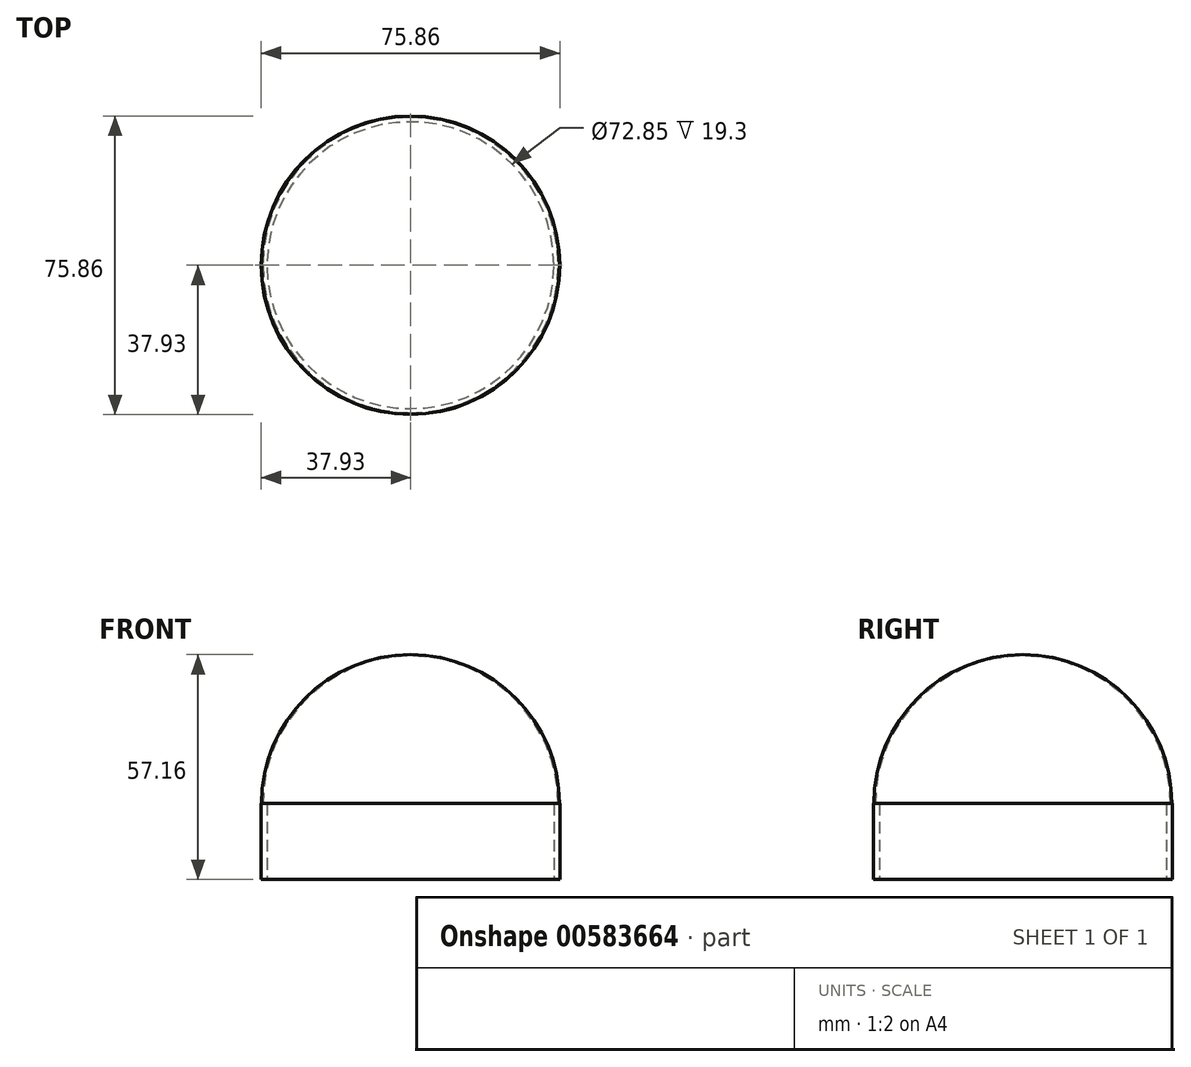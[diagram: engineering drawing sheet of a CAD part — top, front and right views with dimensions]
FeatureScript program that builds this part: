
annotation { "Feature Type Name" : "Feature", "Feature Type Description" : "" }
export const myFeature = defineFeature(function(context is Context, id is Id, definition is map)
    precondition{}
    {
        {
            var Q0;
            Q0=qCreatedBy(makeId("Top.planeOp"),FACE);
            var sketch = newSketch(context, id + "F0", { "sketchPlane" : qUnion([Q0])});
            skCircle(sketch, "E0", {"center": v(0, 0) * mm, "radius": 37.5 * mm});
            skSolve(sketch);
        }
        {
            var Q0;
            Q0=qCreatedBy(makeId("Top.planeOp"),FACE);
            var sketch = newSketch(context, id + "F1", { "sketchPlane" : qUnion([Q0])});
            skCircle(sketch, "E1", {"center": v(0, 0) * mm, "radius": 37.93 * mm});
            skSolve(sketch);
        }
        {
            var Q0;
            Q0 = qSketchRegion(id + "F1", true);
            var Q1;
            Q1=makeQuery(id+"F0.imprint","IMPRINT",FACE,{"disambiguationData":[TD([[makeQuery(id+"F0.imprint","IMPRINT",EDGE,{"derivedFrom":sQuery(id+"F0.wireOp",EDGE,"E0")}),1.0]])]});
            extrude(context, id + "F2", {"entities" : qUnion([Q0, Q1]), "depth" : 19.3 * mm, "offsetDistance" : 25 * mm});
        }
        {
            var Q0;
            Q0=makeQuery(id+"F2.opExtrude","CAP_FACE",FACE,{"disambiguationData":[OSD([sQuery(id+"F0.wireOp",EDGE,"E0")])],"isStart":false});
            var sketch = newSketch(context, id + "F3", { "sketchPlane" : qUnion([Q0])});
            skArc(sketch, "E2", {"start": v(0, -37.86) * mm, "mid": v(37.86, 0) * mm, "end": v(0, 37.86) * mm});
            skLineSegment(sketch, "E3", {"start": v(0, 46.44) * mm, "end": v(0, -50.35) * mm, "construction": true});
            skLineSegment(sketch, "E4", {"start": v(0, 37.86) * mm, "end": v(0, -37.86) * mm});
            skSolve(sketch);
        }
        {
            var Q0;
            {var subQ0=sQuery(id+"F3.wireOp",EDGE,"E2");Q0=makeQuery(id+"F3.imprint","IMPRINT",FACE,{"disambiguationData":[TD([[makeQuery(id+"F3.imprint","IMPRINT",EDGE,{"derivedFrom":subQ0}),1.0]])]});}
            var Q1;
            Q1=sQuery(id+"F3.wireOp",EDGE,"E4");
            revolve(context, id + "F4", {"entities" : qUnion([Q0]), "axis" : qUnion([Q1]), "revolveType" : RevolveType.ONE_DIRECTION, "angle" : 180 * degree});
        }
        {
            var Q0;
            Q0=makeQuery(id+"F2.opExtrude","CAP_FACE",FACE,{"disambiguationData":[OSD([sQuery(id+"F1.wireOp",EDGE,"E1")])],"isStart":true});
            var Q1;
            Q1=makeQuery(id+"F2.opExtrude","CAP_FACE",FACE,{"disambiguationData":[OSD([sQuery(id+"F0.wireOp",EDGE,"E0")])],"isStart":true});
            var Q2;
            Q2=makeQuery(id+"F2.opExtrude","CAP_FACE",FACE,{"disambiguationData":[OSD([sQuery(id+"F1.wireOp",EDGE,"E1")])],"isStart":false});
            shell(context, id + "F5", {"entities" : qUnion([Q0, Q1, Q2]), "thickness" : 1.5 * mm});
        }
        {
            var Q0;
            Q0=makeQuery(id+"F2.opExtrude","SWEPT_BODY",BODY,{"disambiguationData":[OSD([sQuery(id+"F0.wireOp",EDGE,"E0")])]});
            deleteBodies(context, id + "F6", {"entities" : qUnion([Q0])});
        }
    });
